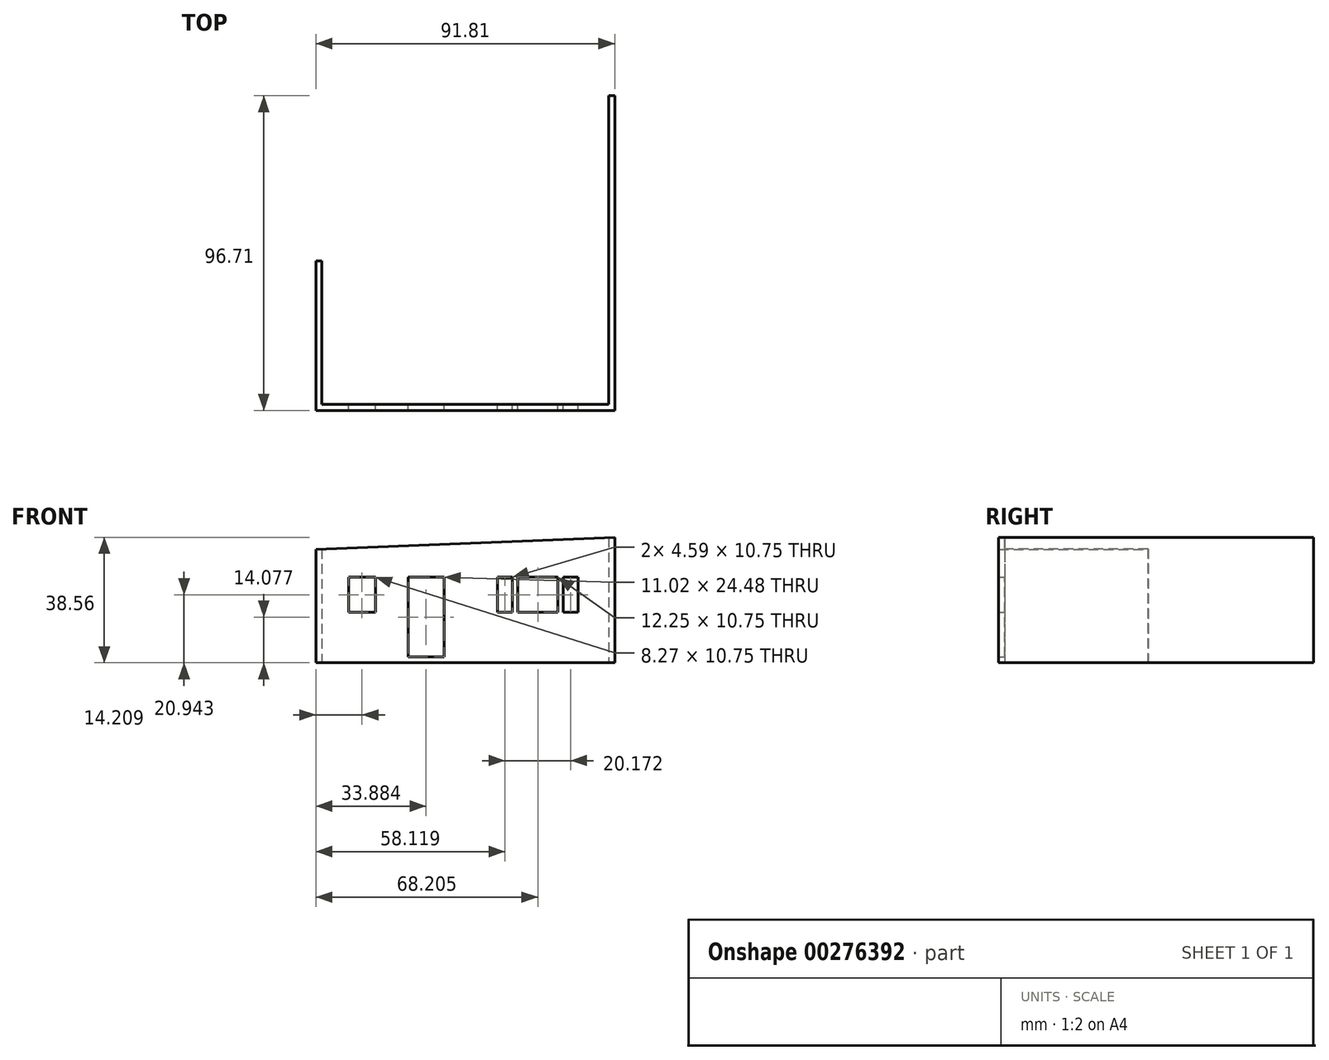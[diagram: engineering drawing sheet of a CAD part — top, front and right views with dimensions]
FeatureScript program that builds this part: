
annotation { "Feature Type Name" : "Feature", "Feature Type Description" : "" }
export const myFeature = defineFeature(function(context is Context, id is Id, definition is map)
    precondition{}
    {
        {
            var Q0;
            Q0=qCreatedBy(makeId("Front.planeOp"),FACE);
            var sketch = newSketch(context, id + "F0", { "sketchPlane" : qUnion([Q0])});
            skLineSegment(sketch, "E0.bottom", {"start": v(-42.93, 0) * mm, "end": v(48.88, 0) * mm});
            skLineSegment(sketch, "E0.left", {"start": v(-42.93, 0) * mm, "end": v(-42.93, 34.89) * mm});
            skLineSegment(sketch, "E0.right", {"start": v(48.88, 0) * mm, "end": v(48.88, 38.56) * mm});
            skLineSegment(sketch, "E1.bottom", {"start": v(-14.55, 1.84) * mm, "end": v(-3.54, 1.84) * mm});
            skLineSegment(sketch, "E1.top", {"start": v(-14.55, 26.32) * mm, "end": v(-3.54, 26.32) * mm});
            skLineSegment(sketch, "E1.left", {"start": v(-14.55, 1.84) * mm, "end": v(-14.55, 26.32) * mm});
            skLineSegment(sketch, "E1.right", {"start": v(-3.54, 1.84) * mm, "end": v(-3.54, 26.32) * mm});
            skLineSegment(sketch, "E2.bottom", {"start": v(-32.85, 26.32) * mm, "end": v(-24.59, 26.32) * mm});
            skLineSegment(sketch, "E2.top", {"start": v(-32.85, 15.57) * mm, "end": v(-24.59, 15.57) * mm});
            skLineSegment(sketch, "E2.left", {"start": v(-32.85, 26.32) * mm, "end": v(-32.85, 15.57) * mm});
            skLineSegment(sketch, "E2.right", {"start": v(-24.59, 26.32) * mm, "end": v(-24.59, 15.57) * mm});
            skLineSegment(sketch, "E3.bottom", {"start": v(12.9, 26.32) * mm, "end": v(17.49, 26.32) * mm});
            skLineSegment(sketch, "E3.top", {"start": v(12.9, 15.57) * mm, "end": v(17.49, 15.57) * mm});
            skLineSegment(sketch, "E3.left", {"start": v(12.9, 26.32) * mm, "end": v(12.9, 15.57) * mm});
            skLineSegment(sketch, "E3.right", {"start": v(17.49, 26.32) * mm, "end": v(17.49, 15.57) * mm});
            skLineSegment(sketch, "E4.bottom", {"start": v(19.15, 26.32) * mm, "end": v(31.4, 26.32) * mm});
            skLineSegment(sketch, "E4.top", {"start": v(19.15, 15.57) * mm, "end": v(31.4, 15.57) * mm});
            skLineSegment(sketch, "E4.left", {"start": v(19.15, 26.32) * mm, "end": v(19.15, 15.57) * mm});
            skLineSegment(sketch, "E4.right", {"start": v(31.4, 26.32) * mm, "end": v(31.4, 15.57) * mm});
            skLineSegment(sketch, "E5", {"start": v(25.27, 25.16) * mm, "end": v(25.27, 15.57) * mm, "construction": true});
            skPoint(sketch, "E5.startSnap0", {"position": v(25.27, 26.32) * mm});
            skLineSegment(sketch, "E6.MirrorCS", {"start": v(37.66, 26.32) * mm, "end": v(33.06, 26.32) * mm});
            skLineSegment(sketch, "E7.MirrorCS", {"start": v(37.66, 15.57) * mm, "end": v(33.06, 15.57) * mm});
            skLineSegment(sketch, "E8.MirrorCS", {"start": v(33.06, 26.32) * mm, "end": v(33.06, 15.57) * mm});
            skLineSegment(sketch, "E9.MirrorCS", {"start": v(37.66, 26.32) * mm, "end": v(37.66, 15.57) * mm});
            skLineSegment(sketch, "E10", {"start": v(-42.93, 34.89) * mm, "end": v(48.88, 38.56) * mm});
            skSolve(sketch);
        }
        {
            var Q0;
            Q0=makeQuery(id+"F0.imprint","IMPRINT",FACE,{"disambiguationData":[TD([[makeQuery(id+"F0.imprint","IMPRINT",EDGE,{"derivedFrom":sQuery(id+"F0.wireOp",EDGE,"E0.bottom")}),1.0]])]});
            extrude(context, id + "F1", {"entities" : qUnion([Q0]), "depth" : 1.84 * mm});
        }
        {
            var Q0;
            Q0=makeQuery(id+"F1.opExtrude","CAP_FACE",FACE,{"disambiguationData":[OSD([sQuery(id+"F0.wireOp",EDGE,"E0.bottom"),sQuery(id+"F0.wireOp",EDGE,"E0.left"),sQuery(id+"F0.wireOp",EDGE,"E0.right"),sQuery(id+"F0.wireOp",EDGE,"E1.bottom"),sQuery(id+"F0.wireOp",EDGE,"E1.top"),sQuery(id+"F0.wireOp",EDGE,"E1.left"),sQuery(id+"F0.wireOp",EDGE,"E1.right"),sQuery(id+"F0.wireOp",EDGE,"E2.bottom"),sQuery(id+"F0.wireOp",EDGE,"E2.top"),sQuery(id+"F0.wireOp",EDGE,"E2.left"),sQuery(id+"F0.wireOp",EDGE,"E2.right"),sQuery(id+"F0.wireOp",EDGE,"E3.bottom"),sQuery(id+"F0.wireOp",EDGE,"E3.top"),sQuery(id+"F0.wireOp",EDGE,"E3.left"),sQuery(id+"F0.wireOp",EDGE,"E3.right"),sQuery(id+"F0.wireOp",EDGE,"E4.bottom"),sQuery(id+"F0.wireOp",EDGE,"E4.top"),sQuery(id+"F0.wireOp",EDGE,"E4.left"),sQuery(id+"F0.wireOp",EDGE,"E4.right"),sQuery(id+"F0.wireOp",EDGE,"E6.MirrorCS"),sQuery(id+"F0.wireOp",EDGE,"E7.MirrorCS"),sQuery(id+"F0.wireOp",EDGE,"E8.MirrorCS"),sQuery(id+"F0.wireOp",EDGE,"E9.MirrorCS"),sQuery(id+"F0.wireOp",EDGE,"E10")])],"isStart":true});
            var sketch = newSketch(context, id + "F2", { "sketchPlane" : qUnion([Q0])});
            skLineSegment(sketch, "E11", {"start": v(42.93, 34.89) * mm, "end": v(42.93, 0) * mm});
            skLineSegment(sketch, "E12", {"start": v(-48.88, 38.56) * mm, "end": v(-48.88, 0) * mm});
            skLineSegment(sketch, "E13.0", {"start": v(41.1, 34.96) * mm, "end": v(41.1, 0) * mm});
            skLineSegment(sketch, "E14.0", {"start": v(-47.05, 38.49) * mm, "end": v(-47.05, 0) * mm});
            skLineSegment(sketch, "E15", {"start": v(42.93, 34.89) * mm, "end": v(41.1, 34.96) * mm});
            skLineSegment(sketch, "E16", {"start": v(41.1, 0) * mm, "end": v(42.93, 0) * mm});
            skPoint(sketch, "E17.orphan", {"position": v(38.41, 0) * mm});
            skLineSegment(sketch, "E18", {"start": v(-48.88, 38.56) * mm, "end": v(-47.05, 38.49) * mm});
            skLineSegment(sketch, "E19", {"start": v(-48.88, 0) * mm, "end": v(-47.05, 0) * mm});
            skSolve(sketch);
        }
        {
            var Q0;
            Q0 = qSketchRegion(id + "F2", true);
            extrude(context, id + "F3", {"entities" : qUnion([Q0]), "operationType" : NewBodyOperationType.ADD, "depth" : 44.07 * mm});
        }
        {
            var Q0;
            Q0=makeQuery(id+"F3.opExtrude","CAP_FACE",FACE,{"disambiguationData":[OSD([sQuery(id+"F2.wireOp",EDGE,"E12"),sQuery(id+"F2.wireOp",EDGE,"E14.0"),sQuery(id+"F2.wireOp",EDGE,"E18"),sQuery(id+"F2.wireOp",EDGE,"E19")])],"isStart":false});
            var sketch = newSketch(context, id + "F4", { "sketchPlane" : qUnion([Q0])});
            skLineSegment(sketch, "E20", {"start": v(-48.88, 38.56) * mm, "end": v(-47.05, 38.49) * mm});
            skLineSegment(sketch, "E21", {"start": v(-47.05, 38.49) * mm, "end": v(-47.05, 0) * mm});
            skLineSegment(sketch, "E22", {"start": v(-47.05, 0) * mm, "end": v(-48.88, 0) * mm});
            skLineSegment(sketch, "E23", {"start": v(-48.88, 0) * mm, "end": v(-48.88, 38.56) * mm});
            skSolve(sketch);
        }
        {
            var Q0;
            Q0 = qSketchRegion(id + "F4", true);
            extrude(context, id + "F5", {"entities" : qUnion([Q0]), "operationType" : NewBodyOperationType.ADD, "depth" : 50.8 * mm});
        }
    });
